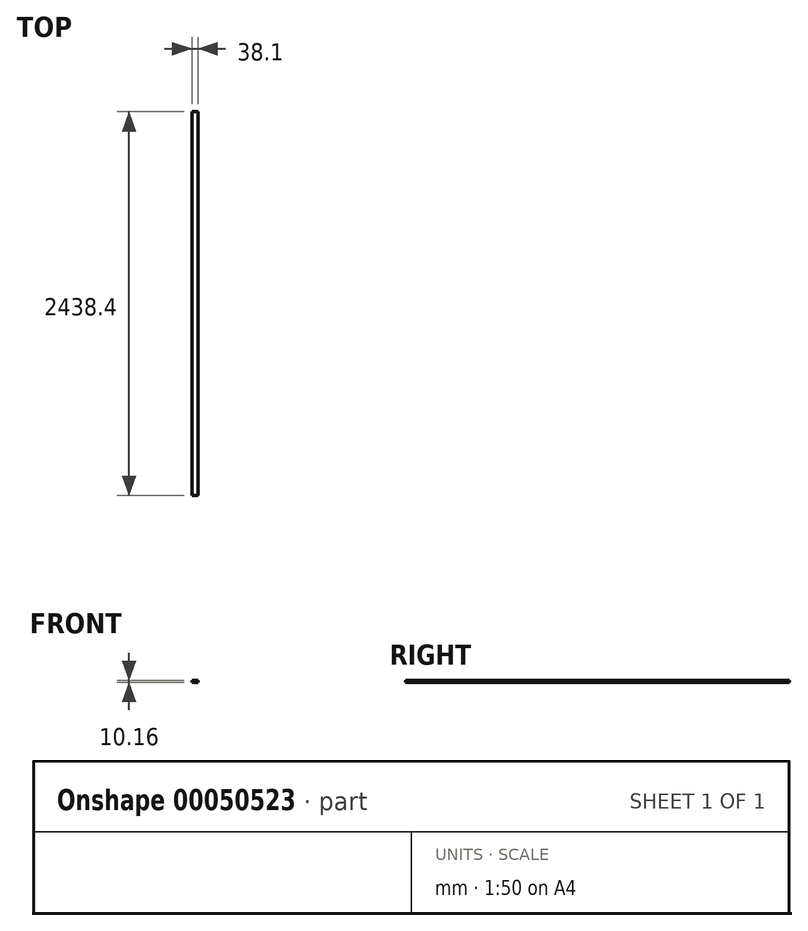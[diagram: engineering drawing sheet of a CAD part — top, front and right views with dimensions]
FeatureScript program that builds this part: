
annotation { "Feature Type Name" : "Feature", "Feature Type Description" : "" }
export const myFeature = defineFeature(function(context is Context, id is Id, definition is map)
    precondition{}
    {
        {
            var Q0;
            Q0=qCreatedBy(makeId("Top.planeOp"),FACE);
            var sketch = newSketch(context, id + "F0", { "sketchPlane" : qUnion([Q0])});
            skLineSegment(sketch, "E0.rect.bottom", {"start": v(19.05, 1219.2) * mm, "end": v(-19.05, 1219.2) * mm});
            skLineSegment(sketch, "E0.rect.top", {"start": v(19.05, -1219.2) * mm, "end": v(-19.05, -1219.2) * mm});
            skLineSegment(sketch, "E0.rect.left", {"start": v(19.05, 1219.2) * mm, "end": v(19.05, -1219.2) * mm});
            skLineSegment(sketch, "E0.rect.right", {"start": v(-19.05, 1219.2) * mm, "end": v(-19.05, -1219.2) * mm});
            skPoint(sketch, "E0.rect.middle", {"position": v(0, 0) * mm});
            skSolve(sketch);
        }
        {
            var Q0;
            Q0=qSketchRegion(id+"F0",true);
            extrude(context, id + "F1", {"entities" : qUnion([Q0]), "endBound" : BoundingType.SYMMETRIC, "depth" : 10.16 * mm});
        }
    });
